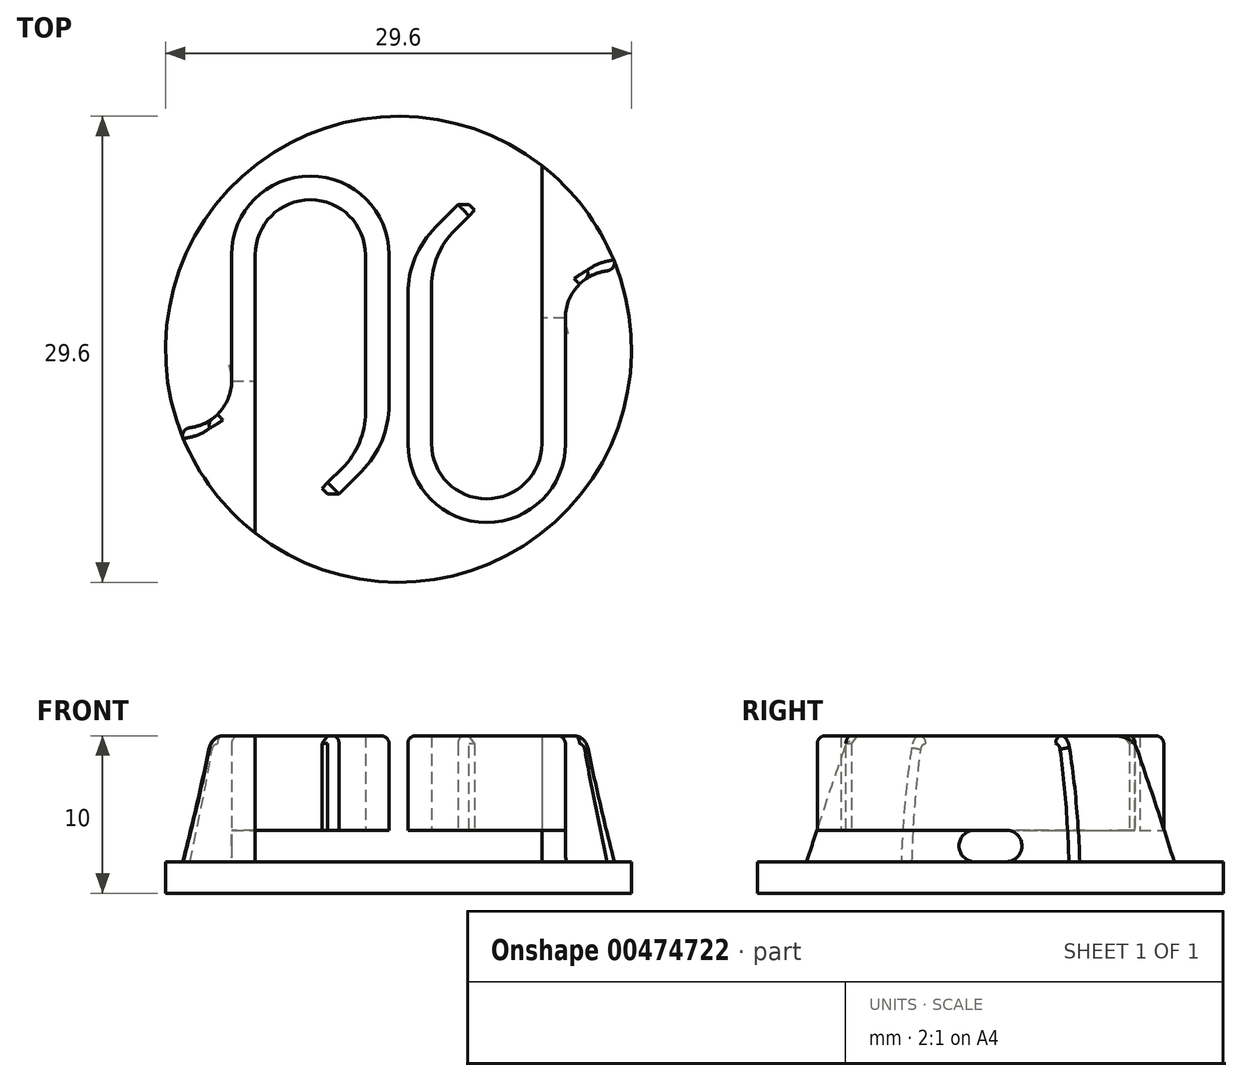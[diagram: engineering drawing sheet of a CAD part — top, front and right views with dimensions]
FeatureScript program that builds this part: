
annotation { "Feature Type Name" : "Feature", "Feature Type Description" : "" }
export const myFeature = defineFeature(function(context is Context, id is Id, definition is map)
    precondition{}
    {
        {
            var Q0;
            Q0=qCreatedBy(makeId("Top.planeOp"),FACE);
            var sketch = newSketch(context, id + "F0", { "sketchPlane" : qUnion([Q0])});
            skCircle(sketch, "E0", {"center": v(0, 0) * mm, "radius": 14.8 * mm});
            skSolve(sketch);
        }
        {
            var Q0;
            Q0 = qSketchRegion(id + "F0", true);
            extrude(context, id + "F1", {"entities" : qUnion([Q0]), "depth" : 2 * mm, "offsetDistance" : 25 * mm});
        }
        {
            var Q0;
            Q0=makeQuery(id+"F1.opExtrude","CAP_FACE",FACE,{"disambiguationData":[OSD([sQuery(id+"F0.wireOp",EDGE,"E0")])],"isStart":false});
            var sketch = newSketch(context, id + "F2", { "sketchPlane" : qUnion([Q0])});
            skLineSegment(sketch, "E1.bottom", {"start": v(-0.75, 9.5) * mm, "end": v(0.75, 9.5) * mm, "construction": true});
            skLineSegment(sketch, "E1.top", {"start": v(-0.75, -9.5) * mm, "end": v(0.75, -9.5) * mm, "construction": true});
            skLineSegment(sketch, "E1.left", {"start": v(-0.75, 9.5) * mm, "end": v(-0.75, -9.5) * mm, "construction": true});
            skLineSegment(sketch, "E1.right", {"start": v(0.75, 9.5) * mm, "end": v(0.75, -9.5) * mm, "construction": true});
            skLineSegment(sketch, "E2", {"start": v(-12.82, -7.4) * mm, "end": v(12.82, 7.4) * mm, "construction": true});
            skLineSegment(sketch, "E3", {"start": v(-0.6, 6) * mm, "end": v(-0.6, -3.51) * mm});
            skLineSegment(sketch, "E4", {"start": v(-2.36, -7.76) * mm, "end": v(-4.14, -9.54) * mm});
            skLineSegment(sketch, "E5", {"start": v(-4.14, -9.54) * mm, "end": v(-4.84, -8.83) * mm});
            skLineSegment(sketch, "E6", {"start": v(-4.84, -8.83) * mm, "end": v(-3.56, -7.55) * mm});
            skLineSegment(sketch, "E7", {"start": v(-2.1, -4.01) * mm, "end": v(-2.1, 6) * mm});
            skArc(sketch, "E8", {"start": v(-0.6, 6) * mm, "mid": v(-5.6, 11) * mm, "end": v(-10.6, 6) * mm});
            skLineSegment(sketch, "E9", {"start": v(-10.6, -2) * mm, "end": v(-10.6, 6) * mm});
            skLineSegment(sketch, "E10", {"start": v(-9.1, -11.67) * mm, "end": v(-9.1, 6) * mm});
            skArc(sketch, "E11", {"start": v(-2.1, 6) * mm, "mid": v(-5.6, 9.5) * mm, "end": v(-9.1, 6) * mm});
            skPoint(sketch, "E12.visualSharp", {"position": v(-2.1, -6.09) * mm});
            skArc(sketch, "E12.filletArc", {"start": v(-3.56, -7.55) * mm, "mid": v(-2.48, -5.93) * mm, "end": v(-2.1, -4.01) * mm});
            skPoint(sketch, "E13.visualSharp", {"position": v(-0.6, -6) * mm});
            skArc(sketch, "E13.filletArc", {"start": v(-2.36, -7.76) * mm, "mid": v(-1.06, -5.81) * mm, "end": v(-0.6, -3.51) * mm});
            skArc(sketch, "E14", {"start": v(-13.94, -4.98) * mm, "mid": v(-11.6, -4.24) * mm, "end": v(-10.6, -2) * mm});
            skArc(sketch, "E15", {"start": v(-13.94, -4.98) * mm, "mid": v(-12, -8.67) * mm, "end": v(-9.1, -11.67) * mm});
            skLineSegment(sketch, "E16", {"start": v(0.6, 3.51) * mm, "end": v(0.6, -6) * mm});
            skArc(sketch, "E17", {"start": v(0.6, -6) * mm, "mid": v(5.6, -11) * mm, "end": v(10.6, -6) * mm});
            skLineSegment(sketch, "E18", {"start": v(2.1, 4.01) * mm, "end": v(2.1, -6) * mm});
            skLineSegment(sketch, "E19", {"start": v(3.56, 7.55) * mm, "end": v(4.84, 8.83) * mm});
            skLineSegment(sketch, "E20", {"start": v(4.84, 8.83) * mm, "end": v(4.14, 9.54) * mm});
            skLineSegment(sketch, "E21", {"start": v(4.14, 9.54) * mm, "end": v(2.36, 7.76) * mm});
            skArc(sketch, "E22", {"start": v(2.1, -6) * mm, "mid": v(5.6, -9.5) * mm, "end": v(9.1, -6) * mm});
            skLineSegment(sketch, "E23", {"start": v(9.1, -6) * mm, "end": v(9.1, 11.67) * mm});
            skLineSegment(sketch, "E24", {"start": v(10.6, -6) * mm, "end": v(10.6, 2) * mm});
            skArc(sketch, "E25", {"start": v(13.94, 4.98) * mm, "mid": v(11.6, 4.24) * mm, "end": v(10.6, 2) * mm});
            skArc(sketch, "E26", {"start": v(13.94, 4.98) * mm, "mid": v(12, 8.67) * mm, "end": v(9.1, 11.67) * mm});
            skPoint(sketch, "E27.visualSharp", {"position": v(2.1, 6.09) * mm});
            skArc(sketch, "E27.filletArc", {"start": v(3.56, 7.55) * mm, "mid": v(2.48, 5.93) * mm, "end": v(2.1, 4.01) * mm});
            skPoint(sketch, "E28.visualSharp", {"position": v(0.6, 6) * mm});
            skArc(sketch, "E28.filletArc", {"start": v(2.36, 7.76) * mm, "mid": v(1.06, 5.81) * mm, "end": v(0.6, 3.51) * mm});
            skSolve(sketch);
        }
        {
            var Q0;
            Q0 = qSketchRegion(id + "F2", true);
            extrude(context, id + "F3", {"entities" : qUnion([Q0]), "operationType" : NewBodyOperationType.ADD, "depth" : 8 * mm, "offsetDistance" : 25 * mm});
        }
        {
            var Q0;
            Q0=makeQuery(id+"F3.opExtrude","SWEPT_FACE",FACE,{"disambiguationData":[OSD([sQuery(id+"F2.wireOp",EDGE,"E16")])]});
            var sketch = newSketch(context, id + "F4", { "sketchPlane" : qUnion([Q0])});
            skLineSegment(sketch, "E29.bottom", {"start": v(-11.67, 2) * mm, "end": v(12.33, 2) * mm});
            skLineSegment(sketch, "E29.top", {"start": v(-11.67, 4) * mm, "end": v(12.33, 4) * mm});
            skLineSegment(sketch, "E29.left", {"start": v(-11.67, 2) * mm, "end": v(-11.67, 4) * mm});
            skLineSegment(sketch, "E29.right", {"start": v(12.33, 2) * mm, "end": v(12.33, 4) * mm});
            skSolve(sketch);
        }
        {
            var Q0;
            Q0 = qSketchRegion(id + "F4", true);
            var Q1;
            Q1=makeQuery(id+"F3.opExtrude","SWEPT_FACE",FACE,{"disambiguationData":[OSD([sQuery(id+"F2.wireOp",EDGE,"E23")])]});
            extrude(context, id + "F5", {"entities" : qUnion([Q0]), "operationType" : NewBodyOperationType.REMOVE, "endBound" : BoundingType.UP_TO_SURFACE, "oppositeDirection" : true, "depth" : 25 * mm, "endBoundEntityFace" : qUnion([Q1]), "offsetDistance" : 25 * mm});
        }
        {
            var Q0;
            Q0=makeQuery(id+"F3.opExtrude","SWEPT_FACE",FACE,{"disambiguationData":[OSD([sQuery(id+"F2.wireOp",EDGE,"E24")])]});
            var sketch = newSketch(context, id + "F6", { "sketchPlane" : qUnion([Q0])});
            skLineSegment(sketch, "E30.bottom", {"start": v(-11.67, 4) * mm, "end": v(2, 4) * mm});
            skLineSegment(sketch, "E30.top", {"start": v(-11.67, 2) * mm, "end": v(2, 2) * mm});
            skLineSegment(sketch, "E30.left", {"start": v(-11.67, 4) * mm, "end": v(-11.67, 2) * mm});
            skLineSegment(sketch, "E30.right", {"start": v(2, 4) * mm, "end": v(2, 2) * mm});
            skSolve(sketch);
        }
        {
            var Q0;
            Q0 = qSketchRegion(id + "F6", true);
            var Q1;
            {var subQ0=sQuery(id+"F2.wireOp",EDGE,"E23");Q1=makeQuery(id+"F5.boolean.opBoolean","MERGE",FACE,{"derivedFrom":[makeQuery(id+"F3.opExtrude","SWEPT_FACE",FACE,{"disambiguationData":[OSD([subQ0])]}),makeQuery(id+"F5.opExtrude","CAP_FACE",FACE,{"disambiguationData":[OSD([subQ0])],"isStart":false})]});}
            extrude(context, id + "F7", {"entities" : qUnion([Q0]), "operationType" : NewBodyOperationType.REMOVE, "endBound" : BoundingType.UP_TO_SURFACE, "oppositeDirection" : true, "depth" : 2 * mm, "endBoundEntityFace" : qUnion([Q1]), "offsetDistance" : 25 * mm});
        }
        {
            var Q0;
            Q0=makeQuery(id+"F3.opExtrude","SWEPT_FACE",FACE,{"disambiguationData":[OSD([sQuery(id+"F2.wireOp",EDGE,"E3")])]});
            var sketch = newSketch(context, id + "F8", { "sketchPlane" : qUnion([Q0])});
            skLineSegment(sketch, "E31.bottom", {"start": v(-11.67, 4) * mm, "end": v(12.33, 4) * mm});
            skLineSegment(sketch, "E31.top", {"start": v(-11.67, 2) * mm, "end": v(12.33, 2) * mm});
            skLineSegment(sketch, "E31.left", {"start": v(-11.67, 4) * mm, "end": v(-11.67, 2) * mm});
            skLineSegment(sketch, "E31.right", {"start": v(12.33, 4) * mm, "end": v(12.33, 2) * mm});
            skSolve(sketch);
        }
        {
            var Q0;
            Q0 = qSketchRegion(id + "F8", true);
            var Q1;
            Q1=makeQuery(id+"F3.opExtrude","SWEPT_FACE",FACE,{"disambiguationData":[OSD([sQuery(id+"F2.wireOp",EDGE,"E10")])]});
            extrude(context, id + "F9", {"entities" : qUnion([Q0]), "operationType" : NewBodyOperationType.REMOVE, "endBound" : BoundingType.UP_TO_SURFACE, "oppositeDirection" : true, "depth" : 25 * mm, "endBoundEntityFace" : qUnion([Q1]), "offsetDistance" : 25 * mm});
        }
        {
            var Q0;
            Q0=makeQuery(id+"F3.opExtrude","SWEPT_FACE",FACE,{"disambiguationData":[OSD([sQuery(id+"F2.wireOp",EDGE,"E9")])]});
            var sketch = newSketch(context, id + "F10", { "sketchPlane" : qUnion([Q0])});
            skLineSegment(sketch, "E32.bottom", {"start": v(-11.67, 4) * mm, "end": v(2, 4) * mm});
            skLineSegment(sketch, "E32.top", {"start": v(-11.67, 2) * mm, "end": v(2, 2) * mm});
            skLineSegment(sketch, "E32.left", {"start": v(-11.67, 4) * mm, "end": v(-11.67, 2) * mm});
            skLineSegment(sketch, "E32.right", {"start": v(2, 4) * mm, "end": v(2, 2) * mm});
            skSolve(sketch);
        }
        {
            var Q0;
            Q0 = qSketchRegion(id + "F10", true);
            var Q1;
            {var subQ0=sQuery(id+"F2.wireOp",EDGE,"E10");Q1=makeQuery(id+"F9.boolean.opBoolean","MERGE",FACE,{"derivedFrom":[makeQuery(id+"F3.opExtrude","SWEPT_FACE",FACE,{"disambiguationData":[OSD([subQ0])]}),makeQuery(id+"F9.opExtrude","CAP_FACE",FACE,{"disambiguationData":[OSD([subQ0])],"isStart":false})]});}
            extrude(context, id + "F11", {"entities" : qUnion([Q0]), "operationType" : NewBodyOperationType.REMOVE, "endBound" : BoundingType.UP_TO_SURFACE, "oppositeDirection" : true, "depth" : 25 * mm, "endBoundEntityFace" : qUnion([Q1]), "offsetDistance" : 25 * mm});
        }
        {
            var Q0;
            Q0=makeQuery(id+"F11.boolean.opBoolean","COPY",EDGE,{"derivedFrom":makeQuery(id+"F11.opExtrude","SWEPT_EDGE",EDGE,{"disambiguationData":[OSD([sQuery(id+"F2.wireOp",EDGE,"E9"),sQuery(id+"F2.wireOp",EDGE,"E14"),sQuery(id+"F10.wireOp",EDGE,"E32.bottom"),sQuery(id+"F10.wireOp",EDGE,"E32.right")])]})});
            var Q1;
            Q1=makeQuery(id+"F11.boolean.opBoolean","COPY",EDGE,{"derivedFrom":makeQuery(id+"F11.opExtrude","SWEPT_EDGE",EDGE,{"disambiguationData":[OSD([sQuery(id+"F10.wireOp",EDGE,"E32.top"),sQuery(id+"F10.wireOp",EDGE,"E32.right")])]})});
            var Q2;
            Q2=makeQuery(id+"F7.boolean.opBoolean","COPY",EDGE,{"derivedFrom":makeQuery(id+"F7.opExtrude","SWEPT_EDGE",EDGE,{"disambiguationData":[OSD([sQuery(id+"F6.wireOp",EDGE,"E30.top"),sQuery(id+"F6.wireOp",EDGE,"E30.right")])]})});
            var Q3;
            Q3=makeQuery(id+"F7.boolean.opBoolean","COPY",EDGE,{"derivedFrom":makeQuery(id+"F7.opExtrude","SWEPT_EDGE",EDGE,{"disambiguationData":[OSD([sQuery(id+"F2.wireOp",EDGE,"E24"),sQuery(id+"F2.wireOp",EDGE,"E25"),sQuery(id+"F6.wireOp",EDGE,"E30.bottom"),sQuery(id+"F6.wireOp",EDGE,"E30.right")])]})});
            var Q4;
            Q4=makeQuery(id+"F3.opExtrude","CAP_EDGE",EDGE,{"disambiguationData":[OSD([sQuery(id+"F2.wireOp",EDGE,"E25")])],"isStart":true});
            var Q5;
            {var subQ0=sQuery(id+"F4.wireOp",EDGE,"E29.bottom");var subQ1=sQuery(id+"F2.wireOp",EDGE,"E16");var subQ3=makeQuery(id+"F4.imprint","INTERSECT",VERTEX,{"derivedFrom":[makeQuery(id+"F3.opExtrude","SWEPT_EDGE",EDGE,{"disambiguationData":[OSD([subQ1,sQuery(id+"F2.wireOp",EDGE,"E28.filletArc")])]}),subQ0]});var subQ4=sQuery(id+"F2.wireOp",EDGE,"E23");Q5=makeQuery(id+"F5.boolean.opBoolean","MERGE",EDGE,{"derivedFrom":[makeQuery(id+"F3.opExtrude","CAP_EDGE",EDGE,{"disambiguationData":[OSD([subQ4])],"isStart":true}),makeQuery(id+"F5.opExtrude","TWEAK_EDGE",EDGE,{"derivedFrom":[makeQuery(id+"F3.opExtrude","SWEPT_FACE",FACE,{"disambiguationData":[OSD([subQ4])]}),makeQuery(id+"F4.imprint","IMPRINT",EDGE,{"disambiguationData":[TD([[makeQuery(id+"F4.imprint","INTERSECT",VERTEX,{"derivedFrom":[subQ0,sQuery(id+"F4.wireOp",EDGE,"E29.left")]}),-1.0]])],"derivedFrom":subQ0}),makeQuery(id+"F4.imprint","IMPRINT",EDGE,{"disambiguationData":[TD([[subQ3,-1.0]])],"derivedFrom":subQ0}),makeQuery(id+"F4.imprint","IMPRINT",EDGE,{"disambiguationData":[TD([[makeQuery(id+"F4.imprint","INTERSECT",VERTEX,{"derivedFrom":[subQ0,sQuery(id+"F4.wireOp",EDGE,"E29.right")]}),1.0]])],"derivedFrom":subQ0})]})]});}
            var Q6;
            Q6=makeQuery(id+"F3.opExtrude","CAP_EDGE",EDGE,{"disambiguationData":[OSD([sQuery(id+"F2.wireOp",EDGE,"E14")])],"isStart":true});
            var Q7;
            {var subQ0=sQuery(id+"F8.wireOp",EDGE,"E31.top");var subQ1=sQuery(id+"F2.wireOp",EDGE,"E3");var subQ2=makeQuery(id+"F8.imprint","INTERSECT",VERTEX,{"derivedFrom":[makeQuery(id+"F3.opExtrude","SWEPT_EDGE",EDGE,{"disambiguationData":[OSD([subQ1,sQuery(id+"F2.wireOp",EDGE,"E8")])]}),subQ0]});var subQ3=makeQuery(id+"F8.imprint","INTERSECT",VERTEX,{"derivedFrom":[makeQuery(id+"F3.opExtrude","SWEPT_EDGE",EDGE,{"disambiguationData":[OSD([subQ1,sQuery(id+"F2.wireOp",EDGE,"E13.filletArc")])]}),subQ0]});var subQ4=sQuery(id+"F2.wireOp",EDGE,"E10");Q7=makeQuery(id+"F9.boolean.opBoolean","MERGE",EDGE,{"derivedFrom":[makeQuery(id+"F3.opExtrude","CAP_EDGE",EDGE,{"disambiguationData":[OSD([subQ4])],"isStart":true}),makeQuery(id+"F9.opExtrude","TWEAK_EDGE",EDGE,{"derivedFrom":[makeQuery(id+"F3.opExtrude","SWEPT_FACE",FACE,{"disambiguationData":[OSD([subQ4])]}),makeQuery(id+"F8.imprint","IMPRINT",EDGE,{"disambiguationData":[TD([[subQ3,1.0],[makeQuery(id+"F8.imprint","INTERSECT",VERTEX,{"derivedFrom":[subQ0,sQuery(id+"F8.wireOp",EDGE,"E31.left")]}),-1.0]])],"derivedFrom":subQ0}),makeQuery(id+"F8.imprint","IMPRINT",EDGE,{"disambiguationData":[TD([[subQ2,-1.0],[subQ3,1.0]])],"derivedFrom":subQ0}),makeQuery(id+"F8.imprint","IMPRINT",EDGE,{"disambiguationData":[TD([[subQ2,-1.0],[makeQuery(id+"F8.imprint","INTERSECT",VERTEX,{"derivedFrom":[subQ0,sQuery(id+"F8.wireOp",EDGE,"E31.right")]}),1.0]])],"derivedFrom":subQ0})]})]});}
            fillet(context, id + "F12", {"entities" : qUnion([Q0, Q1, Q2, Q3, Q4, Q5, Q6, Q7]), "radius" : 1 * mm, "tangentPropagation" : true, "allowEdgeOverflow" : false});
        }
        {
            var Q0;
            Q0=makeQuery(id+"F3.opExtrude","CAP_EDGE",EDGE,{"disambiguationData":[OSD([sQuery(id+"F2.wireOp",EDGE,"E26")])],"isStart":false});
            var Q1;
            Q1=makeQuery(id+"F3.opExtrude","CAP_EDGE",EDGE,{"disambiguationData":[OSD([sQuery(id+"F2.wireOp",EDGE,"E15")])],"isStart":false});
            chamfer(context, id + "F13", {"entities" : qUnion([Q0, Q1]), "chamferType" : ChamferType.TWO_OFFSETS, "width1" : 2 * mm, "oppositeDirection" : false, "width2" : 8 * mm, "tangentPropagation" : true});
        }
        {
            var Q0;
            {var subQ0=sQuery(id+"F2.wireOp",EDGE,"E15");Q0=makeQuery(id+"F13.opChamfer","BLEND_EDGE",EDGE,{"blendedFrom":[makeQuery(id+"F3.opExtrude","CAP_EDGE",EDGE,{"disambiguationData":[OSD([subQ0])],"isStart":false}),makeQuery(id+"F3.opExtrude","CAP_FACE",FACE,{"disambiguationData":[OSD([sQuery(id+"F2.wireOp",EDGE,"E3"),sQuery(id+"F2.wireOp",EDGE,"E4"),sQuery(id+"F2.wireOp",EDGE,"E5"),sQuery(id+"F2.wireOp",EDGE,"E6"),sQuery(id+"F2.wireOp",EDGE,"E7"),sQuery(id+"F2.wireOp",EDGE,"E8"),sQuery(id+"F2.wireOp",EDGE,"E9"),sQuery(id+"F2.wireOp",EDGE,"E10"),sQuery(id+"F2.wireOp",EDGE,"E11"),sQuery(id+"F2.wireOp",EDGE,"E12.filletArc"),sQuery(id+"F2.wireOp",EDGE,"E13.filletArc"),sQuery(id+"F2.wireOp",EDGE,"E14"),subQ0])],"isStart":false})],"blendedInto":[makeQuery(id+"F3.opExtrude","CAP_FACE",FACE,{"disambiguationData":[OSD([sQuery(id+"F2.wireOp",EDGE,"E3"),sQuery(id+"F2.wireOp",EDGE,"E4"),sQuery(id+"F2.wireOp",EDGE,"E5"),sQuery(id+"F2.wireOp",EDGE,"E6"),sQuery(id+"F2.wireOp",EDGE,"E7"),sQuery(id+"F2.wireOp",EDGE,"E8"),sQuery(id+"F2.wireOp",EDGE,"E9"),sQuery(id+"F2.wireOp",EDGE,"E10"),sQuery(id+"F2.wireOp",EDGE,"E11"),sQuery(id+"F2.wireOp",EDGE,"E12.filletArc"),sQuery(id+"F2.wireOp",EDGE,"E13.filletArc"),sQuery(id+"F2.wireOp",EDGE,"E14"),subQ0])],"isStart":false})]});}
            var Q1;
            {var subQ0=sQuery(id+"F2.wireOp",EDGE,"E26");Q1=makeQuery(id+"F13.opChamfer","BLEND_EDGE",EDGE,{"blendedFrom":[makeQuery(id+"F3.opExtrude","CAP_EDGE",EDGE,{"disambiguationData":[OSD([subQ0])],"isStart":false}),makeQuery(id+"F3.opExtrude","CAP_FACE",FACE,{"disambiguationData":[OSD([sQuery(id+"F2.wireOp",EDGE,"E16"),sQuery(id+"F2.wireOp",EDGE,"E17"),sQuery(id+"F2.wireOp",EDGE,"E18"),sQuery(id+"F2.wireOp",EDGE,"E19"),sQuery(id+"F2.wireOp",EDGE,"E20"),sQuery(id+"F2.wireOp",EDGE,"E21"),sQuery(id+"F2.wireOp",EDGE,"E22"),sQuery(id+"F2.wireOp",EDGE,"E23"),sQuery(id+"F2.wireOp",EDGE,"E24"),sQuery(id+"F2.wireOp",EDGE,"E25"),subQ0,sQuery(id+"F2.wireOp",EDGE,"E27.filletArc"),sQuery(id+"F2.wireOp",EDGE,"E28.filletArc")])],"isStart":false})],"blendedInto":[makeQuery(id+"F3.opExtrude","CAP_FACE",FACE,{"disambiguationData":[OSD([sQuery(id+"F2.wireOp",EDGE,"E16"),sQuery(id+"F2.wireOp",EDGE,"E17"),sQuery(id+"F2.wireOp",EDGE,"E18"),sQuery(id+"F2.wireOp",EDGE,"E19"),sQuery(id+"F2.wireOp",EDGE,"E20"),sQuery(id+"F2.wireOp",EDGE,"E21"),sQuery(id+"F2.wireOp",EDGE,"E22"),sQuery(id+"F2.wireOp",EDGE,"E23"),sQuery(id+"F2.wireOp",EDGE,"E24"),sQuery(id+"F2.wireOp",EDGE,"E25"),subQ0,sQuery(id+"F2.wireOp",EDGE,"E27.filletArc"),sQuery(id+"F2.wireOp",EDGE,"E28.filletArc")])],"isStart":false})]});}
            fillet(context, id + "F14", {"entities" : qUnion([Q0, Q1]), "radius" : 1 * mm, "tangentPropagation" : true, "allowEdgeOverflow" : false});
        }
        {
            var Q0;
            Q0=makeQuery(id+"F3.opExtrude","CAP_EDGE",EDGE,{"disambiguationData":[OSD([sQuery(id+"F2.wireOp",EDGE,"E16")])],"isStart":false});
            var Q1;
            Q1=makeQuery(id+"F3.opExtrude","CAP_EDGE",EDGE,{"disambiguationData":[OSD([sQuery(id+"F2.wireOp",EDGE,"E3")])],"isStart":false});
            var Q2;
            Q2=makeQuery(id+"F5.boolean.opBoolean","COPY",EDGE,{"derivedFrom":makeQuery(id+"F5.opExtrude","CAP_EDGE",EDGE,{"disambiguationData":[OSD([sQuery(id+"F4.wireOp",EDGE,"E29.top")])],"isStart":true})});
            var Q3;
            Q3=makeQuery(id+"F9.boolean.opBoolean","COPY",EDGE,{"derivedFrom":makeQuery(id+"F9.opExtrude","CAP_EDGE",EDGE,{"disambiguationData":[OSD([sQuery(id+"F8.wireOp",EDGE,"E31.bottom")])],"isStart":true})});
            fillet(context, id + "F15", {"entities" : qUnion([Q0, Q1, Q2, Q3]), "radius" : 0.5 * mm, "tangentPropagation" : true, "allowEdgeOverflow" : false});
        }
        {
            var Q0;
            Q0=makeQuery(id+"F3.opExtrude","CAP_EDGE",EDGE,{"disambiguationData":[OSD([sQuery(id+"F2.wireOp",EDGE,"E20")])],"isStart":false});
            var Q1;
            Q1=makeQuery(id+"F3.opExtrude","CAP_EDGE",EDGE,{"disambiguationData":[OSD([sQuery(id+"F2.wireOp",EDGE,"E5")])],"isStart":false});
            chamfer(context, id + "F16", {"entities" : qUnion([Q0, Q1]), "width" : 0.5 * mm, "tangentPropagation" : true});
        }
    });
